# Revit family: Window_Shade-Draper-FlexLouver_Rack_Arm_System-Square
name_source: partatom
category: Specialty Equipment
revit_build: Autodesk Revit Architecture 2013 (Build: 20130531_2115(x64)
units: mm (PartAtom-declared; Revit-internal decimal feet)

## types (24) — shared parameters
Description = Non-Retractable Louver System
Louver = Metal - Draper -Aluminum - Silver
Louver Finish Note = The 50A Louvers and 80R Louvers are available in the Silver or White Finish.  The 75E Louvers and 88E Louvers are available in the Natural Anodized or RAL Finish.
Manufacturer = Draper
Model = Square Rack Arm System
Product Name = FlexLouver Rack Arm System
Product Page URL = http://www.draperinc.com
Rack Arms = Metal - Draper - Aluminum
URL = http://www.draperinc.com

## per-type parameters (varying)
| type | 50A Louver | 75E Louver | 80R Louver | 88E Louver | Box Rack Arm | Heavy Duty Rack Arm | LI Location | Louver Bracket Location | Louver Location | Louver Width | Manual Operation | Motorized Operation | Standard Rack Arm |
| Standard-88E-Motorized | No | No | No | Yes | No | No | 3 3/8" | 1 31/32" | 2 1/2" | 3 3/8" | No | Yes | Yes |
| Standard-80R-Motorized | No | No | Yes | No | No | No | 3 1/8" | 1 31/32" | 2 1/4" | 3 1/8" | No | Yes | Yes |
| Standard-75E-Motorized | No | Yes | No | No | No | No | 2 15/16" | 1 31/32" | 2 1/2" | 2 11/16" | No | Yes | Yes |
| Standard-50A-Motorized | Yes | No | No | No | No | No | 1 15/16" | 1 31/32" | 1 3/4" | 1 15/16" | No | Yes | Yes |
| Heavy Duty-88E-Motorized | No | No | No | Yes | No | Yes | 3 3/8" | 4 1/4" | 2 1/2" | 3 3/8" | No | Yes | No |
| Heavy Duty-80R-Motorized | No | No | Yes | No | No | Yes | 3 1/8" | 4 1/4" | 2 1/4" | 3 1/8" | No | Yes | No |
| Heavy Duty-75E-Motorized | No | Yes | No | No | No | Yes | 2 15/16" | 4 1/4" | 2 1/2" | 2 11/16" | No | Yes | No |
| Heavy Duty-50A-Motorized | Yes | No | No | No | No | Yes | 1 15/16" | 4 1/4" | 1 3/4" | 1 15/16" | No | Yes | No |
| Box-88E-Motorized | No | No | No | Yes | Yes | No | 3 3/8" | 5 1/16" | 2 1/2" | 3 3/8" | No | Yes | No |
| Box-80R-Motorized | No | No | Yes | No | Yes | No | 3 1/8" | 5 1/16" | 2 1/4" | 3 1/8" | No | Yes | No |
| Box-75E-Motorized | No | Yes | No | No | Yes | No | 2 15/16" | 5 1/16" | 2 1/2" | 2 11/16" | No | Yes | No |
| Box-50A-Motorized | Yes | No | No | No | Yes | No | 1 15/16" | 5 1/16" | 1 3/4" | 1 15/16" | No | Yes | No |
| Standard-88E-Manual | No | No | No | Yes | No | No | 3 3/8" | 1 31/32" | 2 1/2" | 3 3/8" | Yes | No | Yes |
| Standard-80R-Manual | No | No | Yes | No | No | No | 3 1/8" | 1 31/32" | 2 1/4" | 3 1/8" | Yes | No | Yes |
| Standard-75E-Manual | No | Yes | No | No | No | No | 2 15/16" | 1 31/32" | 2 1/2" | 2 11/16" | Yes | No | Yes |
| Standard-50A-Manual | Yes | No | No | No | No | No | 1 15/16" | 1 31/32" | 1 3/4" | 1 15/16" | Yes | No | Yes |
| Heavy Duty-88E-Manual | No | No | No | Yes | No | Yes | 3 3/8" | 4 1/4" | 2 1/2" | 3 3/8" | Yes | No | No |
| Heavy Duty-80R-Manual | No | No | Yes | No | No | Yes | 3 1/8" | 4 1/4" | 2 1/4" | 3 1/8" | Yes | No | No |
| Heavy Duty-75E-Manual | No | Yes | No | No | No | Yes | 2 15/16" | 4 1/4" | 2 1/2" | 2 11/16" | Yes | No | No |
| Heavy Duty-50A-Manual | Yes | No | No | No | No | Yes | 1 15/16" | 4 1/4" | 1 3/4" | 1 15/16" | Yes | No | No |
| Box-88E-Manual | No | No | No | Yes | Yes | No | 3 3/8" | 5 1/16" | 2 1/2" | 3 3/8" | Yes | No | No |
| Box-80R-Manual | No | No | Yes | No | Yes | No | 3 1/8" | 5 1/16" | 2 1/4" | 3 1/8" | Yes | No | No |
| Box-75E-Manual | No | Yes | No | No | Yes | No | 2 15/16" | 5 1/16" | 2 1/2" | 2 11/16" | Yes | No | No |
| Box-50A-Manual | Yes | No | No | No | Yes | No | 1 15/16" | 5 1/16" | 1 3/4" | 1 15/16" | Yes | No | No |

## geometry (parser evidence)
native form markers: Sweep x19
no freeform markers — native parametric forms only
